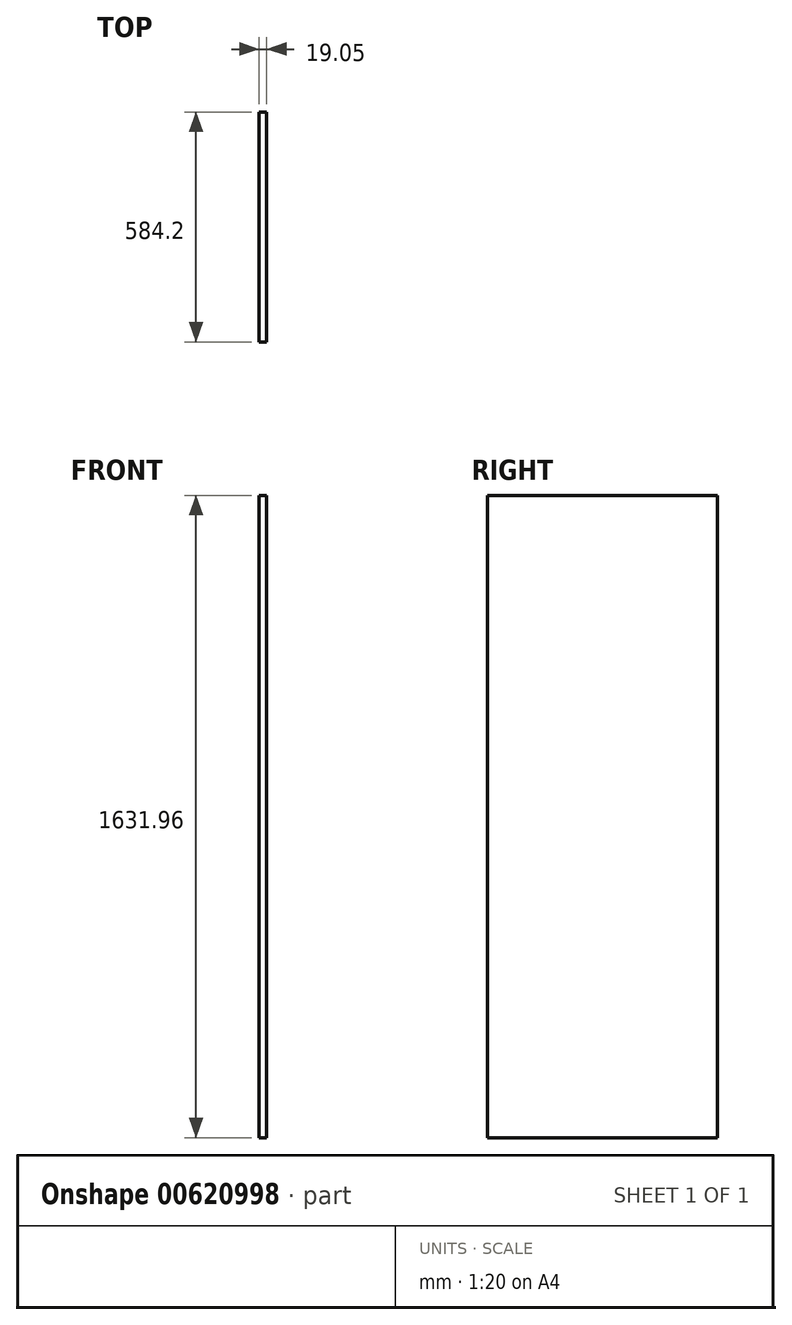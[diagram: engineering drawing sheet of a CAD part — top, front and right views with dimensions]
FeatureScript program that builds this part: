
annotation { "Feature Type Name" : "Feature", "Feature Type Description" : "" }
export const myFeature = defineFeature(function(context is Context, id is Id, definition is map)
    precondition{}
    {
        {
            var Q0;
            Q0=qCreatedBy(makeId("Right.planeOp"),FACE);
            var sketch = newSketch(context, id + "F0", { "sketchPlane" : qUnion([Q0])});
            skLineSegment(sketch, "E0.bottom", {"start": v(292.1, 815.98) * mm, "end": v(-292.1, 815.98) * mm});
            skLineSegment(sketch, "E0.top", {"start": v(292.1, -815.97) * mm, "end": v(-292.1, -815.97) * mm});
            skLineSegment(sketch, "E0.left", {"start": v(292.1, 815.98) * mm, "end": v(292.1, -815.97) * mm});
            skLineSegment(sketch, "E0.right", {"start": v(-292.1, 815.98) * mm, "end": v(-292.1, -815.97) * mm});
            skPoint(sketch, "E0.middle", {"position": v(0, 0) * mm});
            skSolve(sketch);
        }
        {
            var Q0;
            Q0 = qSketchRegion(id + "F0", true);
            extrude(context, id + "F1", {"entities" : qUnion([Q0]), "depth" : 19.05 * mm, "offsetDistance" : 25.4 * mm});
        }
    });
